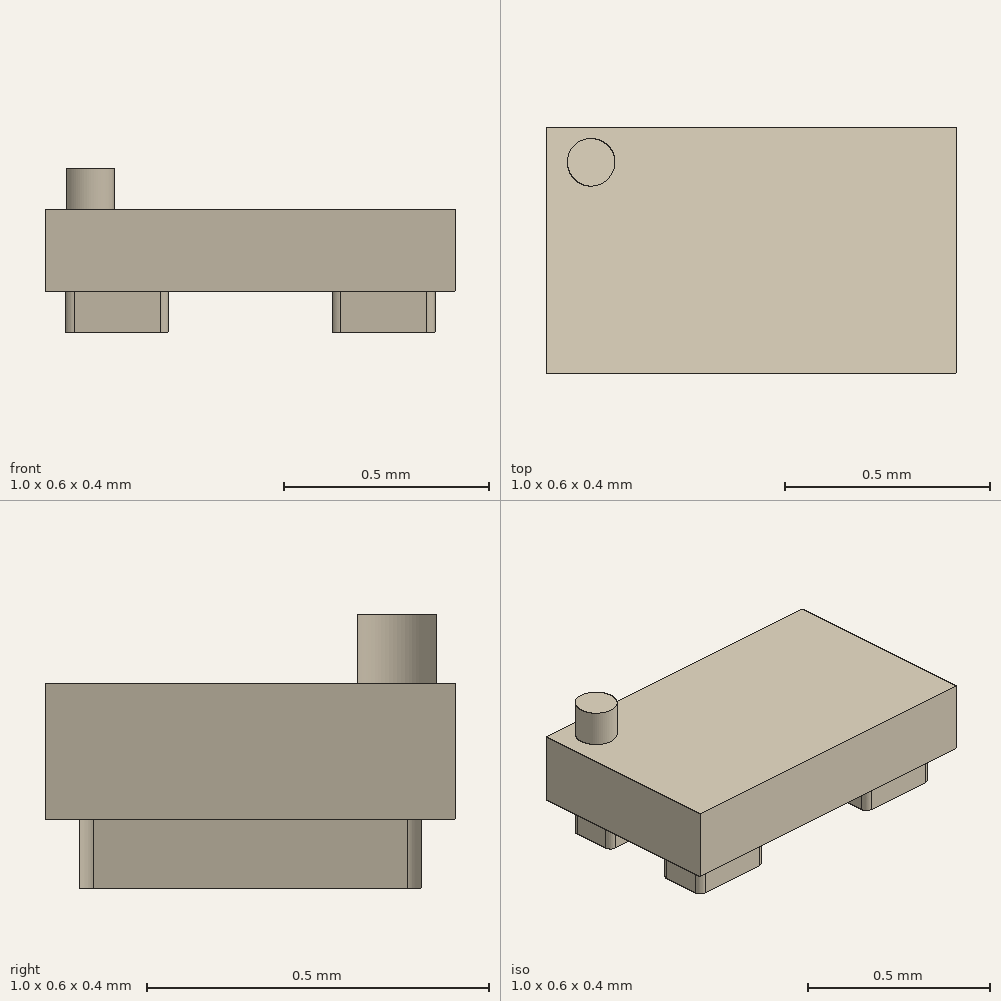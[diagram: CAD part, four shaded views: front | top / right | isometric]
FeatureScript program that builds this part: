
annotation { "Feature Type Name" : "Feature", "Feature Type Description" : "" }
export const myFeature = defineFeature(function(context is Context, id is Id, definition is map)
    precondition{}
    {
        {
            var Q0;
            Q0=qCreatedBy(makeId("Top.planeOp"),FACE);
            var sketch = newSketch(context, id + "F0", { "sketchPlane" : qUnion([Q0])});
            skLineSegment(sketch, "E0.bottom", {"start": v(0.5, -0.3) * mm, "end": v(-0.5, -0.3) * mm});
            skLineSegment(sketch, "E0.top", {"start": v(0.5, 0.3) * mm, "end": v(-0.5, 0.3) * mm});
            skLineSegment(sketch, "E0.left", {"start": v(0.5, -0.3) * mm, "end": v(0.5, 0.3) * mm});
            skLineSegment(sketch, "E0.right", {"start": v(-0.5, -0.3) * mm, "end": v(-0.5, 0.3) * mm});
            skPoint(sketch, "E0.middle", {"position": v(0, 0) * mm});
            skSolve(sketch);
        }
        {
            var Q0;
            Q0 = qSketchRegion(id + "F0", true);
            extrude(context, id + "F1", {"entities" : qUnion([Q0]), "depth" : .2 * mm});
        }
        {
            var Q0;
            Q0=makeQuery(id+"F1.opExtrude","CAP_FACE",FACE,{"disambiguationData":[OSD([sQuery(id+"F0.wireOp",EDGE,"E0.bottom"),sQuery(id+"F0.wireOp",EDGE,"E0.top"),sQuery(id+"F0.wireOp",EDGE,"E0.left"),sQuery(id+"F0.wireOp",EDGE,"E0.right")])],"isStart":true});
            var sketch = newSketch(context, id + "F2", { "sketchPlane" : qUnion([Q0])});
            skLineSegment(sketch, "E1", {"start": v(-0.5, 0) * mm, "end": v(0.5, 0) * mm, "construction": true});
            skLineSegment(sketch, "E2", {"start": v(0, 0.3) * mm, "end": v(0, -0.3) * mm, "construction": true});
            skLineSegment(sketch, "E3.bottom", {"start": v(-0.22, 0.1) * mm, "end": v(-0.43, 0.1) * mm});
            skLineSegment(sketch, "E3.top", {"start": v(-0.22, 0.25) * mm, "end": v(-0.43, 0.25) * mm});
            skLineSegment(sketch, "E3.left", {"start": v(-0.2, 0.12) * mm, "end": v(-0.2, 0.23) * mm});
            skLineSegment(sketch, "E3.right", {"start": v(-0.45, 0.12) * mm, "end": v(-0.45, 0.23) * mm});
            skPoint(sketch, "E3.middle", {"position": v(-0.33, 0.17) * mm});
            skLineSegment(sketch, "E4.bottom", {"start": v(0.22, 0.25) * mm, "end": v(0.43, 0.25) * mm});
            skLineSegment(sketch, "E4.top", {"start": v(0.22, -0.25) * mm, "end": v(0.43, -0.25) * mm});
            skLineSegment(sketch, "E4.left", {"start": v(0.2, 0.23) * mm, "end": v(0.2, -0.23) * mm});
            skLineSegment(sketch, "E4.right", {"start": v(0.45, 0.23) * mm, "end": v(0.45, -0.23) * mm});
            skPoint(sketch, "E4.middle", {"position": v(0.33, 0) * mm});
            skPoint(sketch, "E5.visualSharp", {"position": v(-0.45, 0.25) * mm});
            skArc(sketch, "E5.filletArc", {"start": v(-0.43, 0.25) * mm, "mid": v(-0.44, 0.24) * mm, "end": v(-0.45, 0.23) * mm});
            skPoint(sketch, "E6.visualSharp", {"position": v(-0.2, 0.25) * mm});
            skArc(sketch, "E6.filletArc", {"start": v(-0.2, 0.23) * mm, "mid": v(-0.2, 0.24) * mm, "end": v(-0.22, 0.25) * mm});
            skPoint(sketch, "E7.visualSharp", {"position": v(-0.2, 0.1) * mm});
            skArc(sketch, "E7.filletArc", {"start": v(-0.22, 0.1) * mm, "mid": v(-0.2, 0.1) * mm, "end": v(-0.2, 0.12) * mm});
            skPoint(sketch, "E8.visualSharp", {"position": v(-0.45, 0.1) * mm});
            skArc(sketch, "E8.filletArc", {"start": v(-0.45, 0.12) * mm, "mid": v(-0.44, 0.1) * mm, "end": v(-0.43, 0.1) * mm});
            skArc(sketch, "E9.MirrorCS", {"start": v(-0.43, -0.25) * mm, "mid": v(-0.44, -0.24) * mm, "end": v(-0.45, -0.23) * mm});
            skArc(sketch, "E10.MirrorCS", {"start": v(-0.22, -0.1) * mm, "mid": v(-0.2, -0.1) * mm, "end": v(-0.2, -0.12) * mm});
            skArc(sketch, "E11.MirrorCS", {"start": v(-0.2, -0.23) * mm, "mid": v(-0.2, -0.24) * mm, "end": v(-0.22, -0.25) * mm});
            skArc(sketch, "E12.MirrorCS", {"start": v(-0.45, -0.12) * mm, "mid": v(-0.44, -0.1) * mm, "end": v(-0.43, -0.1) * mm});
            skPoint(sketch, "E13.MirrorP", {"position": v(-0.2, -0.25) * mm});
            skLineSegment(sketch, "E14.MirrorCS", {"start": v(-0.22, -0.1) * mm, "end": v(-0.43, -0.1) * mm});
            skLineSegment(sketch, "E15.MirrorCS", {"start": v(-0.22, -0.25) * mm, "end": v(-0.43, -0.25) * mm});
            skLineSegment(sketch, "E16.MirrorCS", {"start": v(-0.2, -0.12) * mm, "end": v(-0.2, -0.23) * mm});
            skPoint(sketch, "E17.MirrorP", {"position": v(-0.45, -0.25) * mm});
            skPoint(sketch, "E18.MirrorP", {"position": v(-0.33, -0.17) * mm});
            skPoint(sketch, "E19.MirrorP", {"position": v(-0.2, -0.1) * mm});
            skPoint(sketch, "E20.MirrorP", {"position": v(-0.45, -0.1) * mm});
            skLineSegment(sketch, "E21.MirrorCS", {"start": v(-0.45, -0.12) * mm, "end": v(-0.45, -0.23) * mm});
            skPoint(sketch, "E22.visualSharp", {"position": v(0.2, 0.25) * mm});
            skArc(sketch, "E22.filletArc", {"start": v(0.22, 0.25) * mm, "mid": v(0.2, 0.24) * mm, "end": v(0.2, 0.23) * mm});
            skPoint(sketch, "E23.visualSharp", {"position": v(0.45, 0.25) * mm});
            skArc(sketch, "E23.filletArc", {"start": v(0.45, 0.23) * mm, "mid": v(0.44, 0.24) * mm, "end": v(0.43, 0.25) * mm});
            skPoint(sketch, "E24.visualSharp", {"position": v(0.45, -0.25) * mm});
            skArc(sketch, "E24.filletArc", {"start": v(0.43, -0.25) * mm, "mid": v(0.44, -0.24) * mm, "end": v(0.45, -0.23) * mm});
            skPoint(sketch, "E25.visualSharp", {"position": v(0.2, -0.25) * mm});
            skArc(sketch, "E25.filletArc", {"start": v(0.2, -0.23) * mm, "mid": v(0.2, -0.24) * mm, "end": v(0.22, -0.25) * mm});
            skSolve(sketch);
        }
        {
            var Q0;
            Q0 = qSketchRegion(id + "F2", true);
            extrude(context, id + "F3", {"entities" : qUnion([Q0]), "depth" : .1 * mm});
        }
        {
            var Q0;
            Q0=makeQuery(id+"F1.opExtrude","CAP_FACE",FACE,{"disambiguationData":[OSD([sQuery(id+"F0.wireOp",EDGE,"E0.bottom"),sQuery(id+"F0.wireOp",EDGE,"E0.top"),sQuery(id+"F0.wireOp",EDGE,"E0.left"),sQuery(id+"F0.wireOp",EDGE,"E0.right")])],"isStart":false});
            var sketch = newSketch(context, id + "F4", { "sketchPlane" : qUnion([Q0])});
            skCircle(sketch, "E26", {"center": v(-0.4, 0.21) * mm, "radius": 0.06 * mm});
            skSolve(sketch);
        }
        {
            var Q0;
            Q0 = qSketchRegion(id + "F4", true);
            extrude(context, id + "F5", {"entities" : qUnion([Q0]), "depth" : .1 * mm});
        }
    });
